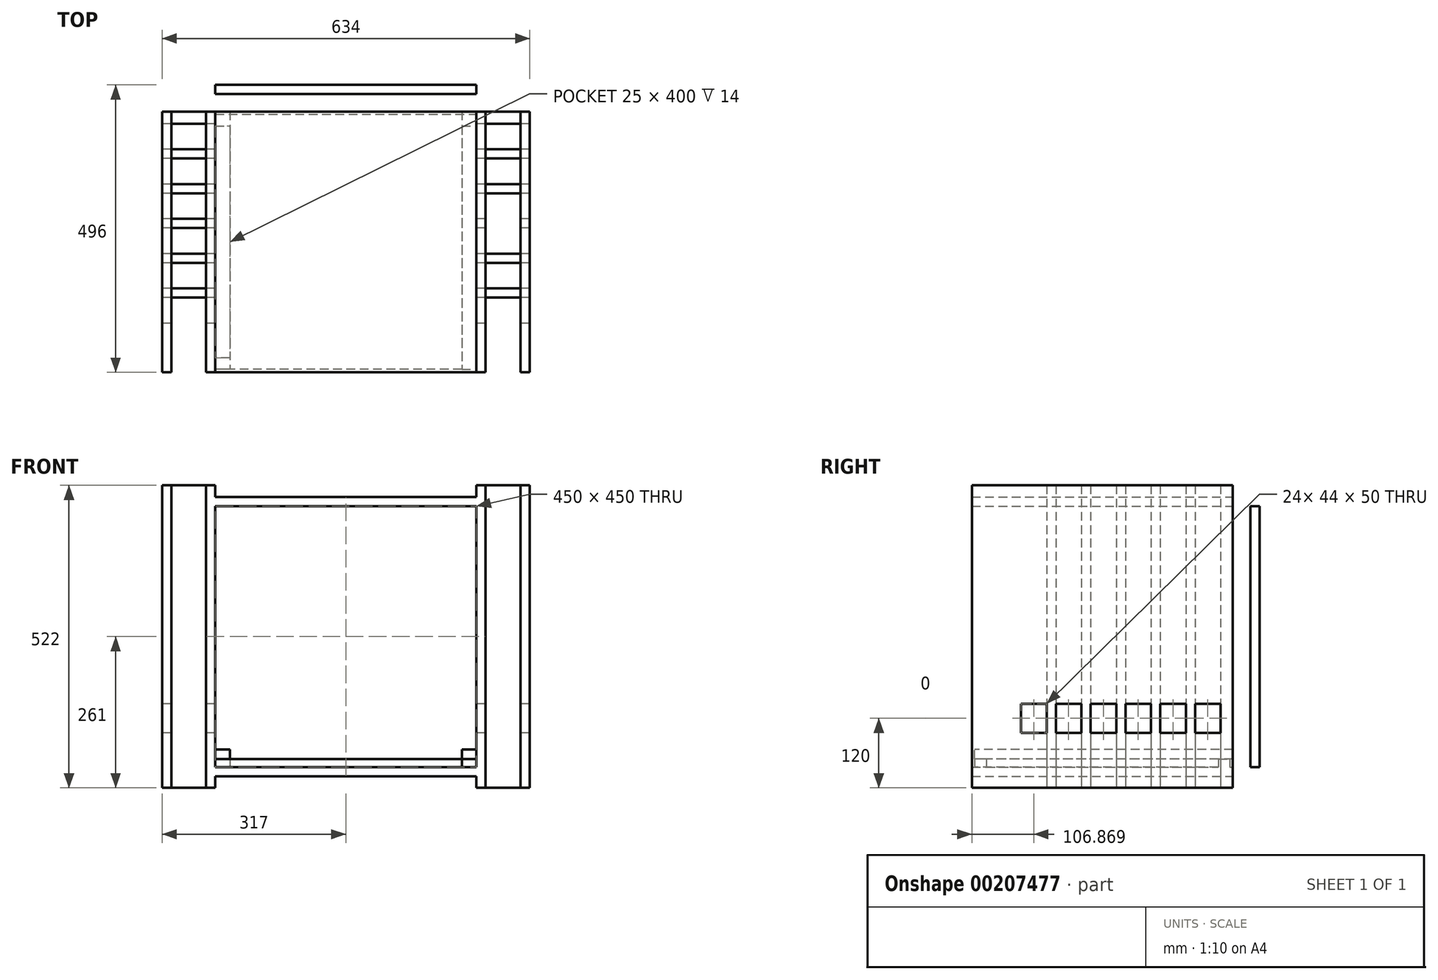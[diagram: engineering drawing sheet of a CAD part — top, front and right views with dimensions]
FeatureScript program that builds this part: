
annotation { "Feature Type Name" : "Feature", "Feature Type Description" : "" }
export const myFeature = defineFeature(function(context is Context, id is Id, definition is map)
    precondition{}
    {
        {
            var Q0;
            Q0=qCreatedBy(makeId("Front.planeOp"),FACE);
            var sketch = newSketch(context, id + "F0", { "sketchPlane" : qUnion([Q0])});
            skLineSegment(sketch, "E0.bottom", {"start": v(0, 0) * mm, "end": v(1200, 0) * mm, "construction": true});
            skLineSegment(sketch, "E0.top", {"start": v(0, 1200) * mm, "end": v(1200, 1200) * mm, "construction": true});
            skLineSegment(sketch, "E0.left", {"start": v(0, 0) * mm, "end": v(0, 1200) * mm, "construction": true});
            skLineSegment(sketch, "E0.right", {"start": v(1200, 0) * mm, "end": v(1200, 1200) * mm, "construction": true});
            skLineSegment(sketch, "E1.bottom", {"start": v(0, 0) * mm, "end": v(50, 0) * mm, "construction": true});
            skLineSegment(sketch, "E1.top", {"start": v(0, 50) * mm, "end": v(50, 50) * mm, "construction": true});
            skLineSegment(sketch, "E1.left", {"start": v(0, 0) * mm, "end": v(0, 50) * mm, "construction": true});
            skLineSegment(sketch, "E1.right", {"start": v(50, 0) * mm, "end": v(50, 50) * mm, "construction": true});
            skPoint(sketch, "E2", {"position": v(50, 50) * mm});
            skLineSegment(sketch, "E3", {"start": v(-443.22, -344.23) * mm, "end": v(-427.22, -344.23) * mm, "construction": true});
            skLineSegment(sketch, "E4", {"start": v(-345.47, -205) * mm, "end": v(-345.47, -221) * mm, "construction": true});
            skLineSegment(sketch, "E5", {"start": v(-341.02, 423.4) * mm, "end": v(-341.02, 407.4) * mm, "construction": true});
            skLineSegment(sketch, "E6", {"start": v(1457.06, 1178.81) * mm, "end": v(1457.06, 1162.81) * mm, "construction": true});
            skLineSegment(sketch, "E7", {"start": v(781.58, 762.66) * mm, "end": v(797.58, 762.66) * mm, "construction": true});
            skSolve(sketch);
        }
        {
            var Q0;
            Q0=qCreatedBy(makeId("Front.planeOp"),FACE);
            var sketch = newSketch(context, id + "F1", { "sketchPlane" : qUnion([Q0])});
            skLineSegment(sketch, "E8.bottom", {"start": v(50, 50) * mm, "end": v(66, 50) * mm});
            skLineSegment(sketch, "E8.top", {"start": v(50, 572) * mm, "end": v(66, 572) * mm});
            skLineSegment(sketch, "E8.left", {"start": v(50, 50) * mm, "end": v(50, 572) * mm});
            skLineSegment(sketch, "E8.right", {"start": v(66, 50) * mm, "end": v(66, 572) * mm});
            skLineSegment(sketch, "E9.bottom", {"start": v(66, 536) * mm, "end": v(516, 536) * mm});
            skLineSegment(sketch, "E9.top", {"start": v(66, 552) * mm, "end": v(516, 552) * mm});
            skLineSegment(sketch, "E9.left", {"start": v(66, 536) * mm, "end": v(66, 552) * mm});
            skLineSegment(sketch, "E9.right", {"start": v(516, 536) * mm, "end": v(516, 552) * mm});
            skLineSegment(sketch, "E10.bottom", {"start": v(66, 70) * mm, "end": v(516, 70) * mm});
            skLineSegment(sketch, "E10.top", {"start": v(66, 86) * mm, "end": v(516, 86) * mm});
            skLineSegment(sketch, "E10.left", {"start": v(66, 70) * mm, "end": v(66, 86) * mm});
            skLineSegment(sketch, "E10.right", {"start": v(516, 70) * mm, "end": v(516, 86) * mm});
            skLineSegment(sketch, "E11.bottom", {"start": v(-10, 572) * mm, "end": v(-26, 572) * mm});
            skLineSegment(sketch, "E11.top", {"start": v(-10, 50) * mm, "end": v(-26, 50) * mm});
            skLineSegment(sketch, "E11.left", {"start": v(-10, 572) * mm, "end": v(-10, 50) * mm});
            skLineSegment(sketch, "E11.right", {"start": v(-26, 572) * mm, "end": v(-26, 50) * mm});
            skLineSegment(sketch, "E12", {"start": v(291, -118.69) * mm, "end": v(291, -340.53) * mm, "construction": true});
            skPoint(sketch, "E12.startSnap0", {"position": v(291, 70) * mm});
            skLineSegment(sketch, "E13.MirrorCS", {"start": v(516, 50) * mm, "end": v(516, 572) * mm});
            skLineSegment(sketch, "E14.MirrorCS", {"start": v(532, 50) * mm, "end": v(532, 572) * mm});
            skLineSegment(sketch, "E15.MirrorCS", {"start": v(532, 572) * mm, "end": v(516, 572) * mm});
            skLineSegment(sketch, "E16.MirrorCS", {"start": v(532, 50) * mm, "end": v(516, 50) * mm});
            skLineSegment(sketch, "E17.MirrorCS", {"start": v(592, 572) * mm, "end": v(592, 50) * mm});
            skLineSegment(sketch, "E18.MirrorCS", {"start": v(592, 50) * mm, "end": v(608, 50) * mm});
            skLineSegment(sketch, "E19.MirrorCS", {"start": v(592, 572) * mm, "end": v(608, 572) * mm});
            skLineSegment(sketch, "E20.MirrorCS", {"start": v(608, 572) * mm, "end": v(608, 50) * mm});
            skPoint(sketch, "E21", {"position": v(66, 692.57) * mm});
            skPoint(sketch, "E22", {"position": v(66, 311) * mm});
            skSolve(sketch);
        }
        {
            var Q0;
            Q0=qCreatedBy(makeId("Top.planeOp"),FACE);
            var sketch = newSketch(context, id + "F2", { "sketchPlane" : qUnion([Q0])});
            skLineSegment(sketch, "E23.bottom", {"start": v(50, 0) * mm, "end": v(66, 0) * mm});
            skLineSegment(sketch, "E23.top", {"start": v(50, -450) * mm, "end": v(66, -450) * mm});
            skLineSegment(sketch, "E23.left", {"start": v(50, 0) * mm, "end": v(50, -450) * mm});
            skLineSegment(sketch, "E23.right", {"start": v(66, 0) * mm, "end": v(66, -450) * mm});
            skLineSegment(sketch, "E24", {"start": v(291, -589.17) * mm, "end": v(291, -887.41) * mm, "construction": true});
            skLineSegment(sketch, "E25.MirrorCS", {"start": v(516, 0) * mm, "end": v(516, -450) * mm});
            skLineSegment(sketch, "E26.MirrorCS", {"start": v(532, 0) * mm, "end": v(532, -450) * mm});
            skLineSegment(sketch, "E27.MirrorCS", {"start": v(532, -450) * mm, "end": v(516, -450) * mm});
            skLineSegment(sketch, "E28.MirrorCS", {"start": v(532, 0) * mm, "end": v(516, 0) * mm});
            skSolve(sketch);
        }
        {
            var Q0;
            {var subQ0=sQuery(id+"F1.wireOp",EDGE,"E10.bottom");Q0=makeQuery(id+"F1.imprint","IMPRINT",FACE,{"disambiguationData":[TD([[makeQuery(id+"F1.imprint","IMPRINT",EDGE,{"derivedFrom":subQ0}),1.0]])]});}
            var Q1;
            Q1=makeQuery(id+"F1.imprint","IMPRINT",FACE,{"disambiguationData":[TD([[makeQuery(id+"F1.imprint","IMPRINT",EDGE,{"derivedFrom":sQuery(id+"F1.wireOp",EDGE,"E14.MirrorCS")}),1.0]])]});
            var Q2;
            {var subQ0=sQuery(id+"F1.wireOp",EDGE,"E9.bottom");Q2=makeQuery(id+"F1.imprint","IMPRINT",FACE,{"disambiguationData":[TD([[makeQuery(id+"F1.imprint","IMPRINT",EDGE,{"derivedFrom":subQ0}),1.0]])]});}
            var Q3;
            Q3=makeQuery(id+"F1.imprint","IMPRINT",FACE,{"disambiguationData":[TD([[makeQuery(id+"F1.imprint","IMPRINT",EDGE,{"derivedFrom":sQuery(id+"F1.wireOp",EDGE,"E17.MirrorCS")}),1.0]])]});
            var Q4;
            {var subQ1=sQuery(id+"F1.wireOp",EDGE,"E8.bottom");Q4=makeQuery(id+"F1.imprint","IMPRINT",FACE,{"disambiguationData":[TD([[makeQuery(id+"F1.imprint","IMPRINT",EDGE,{"derivedFrom":subQ1}),1.0]])]});}
            var Q5;
            Q5=makeQuery(id+"F1.imprint","IMPRINT",FACE,{"disambiguationData":[TD([[makeQuery(id+"F1.imprint","IMPRINT",EDGE,{"derivedFrom":sQuery(id+"F1.wireOp",EDGE,"E11.bottom")}),1.0]])]});
            var Q6;
            Q6=sQuery(id+"F2.wireOp",VERTEX,"E23.left.end");
            extrude(context, id + "F3", {"entities" : qUnion([Q0, Q1, Q2, Q3, Q4, Q5]), "endBound" : BoundingType.UP_TO_VERTEX, "endBoundEntityVertex" : qUnion([Q6]), "depth" : 25 * mm});
        }
        {
            var Q0;
            Q0=qCreatedBy(makeId("Right.planeOp"),FACE);
            var sketch = newSketch(context, id + "F4", { "sketchPlane" : qUnion([Q0])});
            skLineSegment(sketch, "E29.bottom", {"start": v(0, 145) * mm, "end": v(-450, 145) * mm});
            skLineSegment(sketch, "E29.top", {"start": v(0, 195) * mm, "end": v(-450, 195) * mm});
            skLineSegment(sketch, "E29.left", {"start": v(0, 145) * mm, "end": v(0, 195) * mm});
            skLineSegment(sketch, "E29.right", {"start": v(-450, 145) * mm, "end": v(-450, 195) * mm});
            skPoint(sketch, "E30", {"position": v(0, 170) * mm});
            skLineSegment(sketch, "E31.bottom", {"start": v(-5.13, 195) * mm, "end": v(-21.13, 195) * mm});
            skLineSegment(sketch, "E31.top", {"start": v(-5.13, 145) * mm, "end": v(-21.13, 145) * mm});
            skLineSegment(sketch, "E31.left", {"start": v(-5.13, 195) * mm, "end": v(-5.13, 145) * mm});
            skLineSegment(sketch, "E31.right", {"start": v(-21.13, 195) * mm, "end": v(-21.13, 145) * mm});
            skLineSegment(sketch, "E32.1.0.0", {"start": v(-81.13, 195) * mm, "end": v(-81.13, 145) * mm});
            skLineSegment(sketch, "E32.1.0.1", {"start": v(-65.13, 195) * mm, "end": v(-65.13, 145) * mm});
            skLineSegment(sketch, "E32.2.0.0", {"start": v(-141.13, 195) * mm, "end": v(-141.13, 145) * mm});
            skLineSegment(sketch, "E32.2.0.1", {"start": v(-125.13, 195) * mm, "end": v(-125.13, 145) * mm});
            skLineSegment(sketch, "E32.3.0.0", {"start": v(-201.13, 195) * mm, "end": v(-201.13, 145) * mm});
            skLineSegment(sketch, "E32.3.0.1", {"start": v(-185.13, 195) * mm, "end": v(-185.13, 145) * mm});
            skLineSegment(sketch, "E32.4.0.0", {"start": v(-261.13, 195) * mm, "end": v(-261.13, 145) * mm});
            skLineSegment(sketch, "E32.4.0.1", {"start": v(-245.13, 195) * mm, "end": v(-245.13, 145) * mm});
            skLineSegment(sketch, "E32.5.0.0", {"start": v(-321.13, 195) * mm, "end": v(-321.13, 145) * mm});
            skLineSegment(sketch, "E32.5.0.1", {"start": v(-305.13, 195) * mm, "end": v(-305.13, 145) * mm});
            skLineSegment(sketch, "E32.direction1", {"start": v(-21.13, 145) * mm, "end": v(-81.13, 145) * mm, "construction": true});
            skLineSegment(sketch, "E33.0.6.0", {"start": v(-381.13, 195) * mm, "end": v(-381.13, 145) * mm});
            skLineSegment(sketch, "E33.3.6.0", {"start": v(-365.13, 195) * mm, "end": v(-365.13, 145) * mm});
            skSolve(sketch);
        }
        {
            var Q0;
            {var subQ0=sQuery(id+"F4.wireOp",EDGE,"E31.right");Q0=makeQuery(id+"F4.imprint","IMPRINT",FACE,{"disambiguationData":[TD([[makeQuery(id+"F4.imprint","IMPRINT",EDGE,{"derivedFrom":subQ0}),-1.0]])]});}
            var Q1;
            {var subQ0=sQuery(id+"F4.wireOp",EDGE,"E32.1.0.0");Q1=makeQuery(id+"F4.imprint","IMPRINT",FACE,{"disambiguationData":[TD([[makeQuery(id+"F4.imprint","IMPRINT",EDGE,{"derivedFrom":subQ0}),-1.0]])]});}
            var Q2;
            {var subQ0=sQuery(id+"F4.wireOp",EDGE,"E32.2.0.0");Q2=makeQuery(id+"F4.imprint","IMPRINT",FACE,{"disambiguationData":[TD([[makeQuery(id+"F4.imprint","IMPRINT",EDGE,{"derivedFrom":subQ0}),-1.0]])]});}
            var Q3;
            {var subQ0=sQuery(id+"F4.wireOp",EDGE,"E32.3.0.0");Q3=makeQuery(id+"F4.imprint","IMPRINT",FACE,{"disambiguationData":[TD([[makeQuery(id+"F4.imprint","IMPRINT",EDGE,{"derivedFrom":subQ0}),-1.0]])]});}
            var Q4;
            {var subQ0=sQuery(id+"F4.wireOp",EDGE,"E32.4.0.0");Q4=makeQuery(id+"F4.imprint","IMPRINT",FACE,{"disambiguationData":[TD([[makeQuery(id+"F4.imprint","IMPRINT",EDGE,{"derivedFrom":subQ0}),-1.0]])]});}
            var Q5;
            {var subQ0=sQuery(id+"F4.wireOp",EDGE,"E32.5.0.0");Q5=makeQuery(id+"F4.imprint","IMPRINT",FACE,{"disambiguationData":[TD([[makeQuery(id+"F4.imprint","IMPRINT",EDGE,{"derivedFrom":subQ0}),-1.0]])]});}
            extrude(context, id + "F5", {"entities" : qUnion([Q0, Q1, Q2, Q3, Q4, Q5]), "operationType" : NewBodyOperationType.REMOVE, "depth" : 1209 * mm, "hasSecondDirection" : true, "secondDirectionOppositeDirection" : true, "secondDirectionDepth" : 175 * mm});
        }
        {
            var Q0;
            Q0=qCreatedBy(makeId("Top.planeOp"),FACE);
            var sketch = newSketch(context, id + "F6", { "sketchPlane" : qUnion([Q0])});
            skLineSegment(sketch, "E34.bottom", {"start": v(-10, -21.13) * mm, "end": v(50, -21.13) * mm});
            skLineSegment(sketch, "E34.top", {"start": v(-10, -65.13) * mm, "end": v(50, -65.13) * mm});
            skLineSegment(sketch, "E34.left", {"start": v(50, -21.13) * mm, "end": v(50, -65.13) * mm});
            skLineSegment(sketch, "E34.right", {"start": v(-10, -21.13) * mm, "end": v(-10, -65.13) * mm});
            skLineSegment(sketch, "E35.bottom", {"start": v(-10, -81.13) * mm, "end": v(50, -81.13) * mm});
            skLineSegment(sketch, "E35.top", {"start": v(-10, -125.13) * mm, "end": v(50, -125.13) * mm});
            skLineSegment(sketch, "E35.left", {"start": v(50, -81.13) * mm, "end": v(50, -125.13) * mm});
            skLineSegment(sketch, "E35.right", {"start": v(-10, -81.13) * mm, "end": v(-10, -125.13) * mm});
            skLineSegment(sketch, "E36.bottom", {"start": v(50, -141.13) * mm, "end": v(-10, -141.13) * mm});
            skLineSegment(sketch, "E36.top", {"start": v(50, -185.13) * mm, "end": v(-10, -185.13) * mm});
            skLineSegment(sketch, "E36.left", {"start": v(-10, -141.13) * mm, "end": v(-10, -185.13) * mm});
            skLineSegment(sketch, "E36.right", {"start": v(50, -141.13) * mm, "end": v(50, -185.13) * mm});
            skLineSegment(sketch, "E37.bottom", {"start": v(-10, -201.13) * mm, "end": v(50, -201.13) * mm});
            skLineSegment(sketch, "E37.top", {"start": v(-10, -245.13) * mm, "end": v(50, -245.13) * mm});
            skLineSegment(sketch, "E37.left", {"start": v(50, -201.13) * mm, "end": v(50, -245.13) * mm});
            skLineSegment(sketch, "E37.right", {"start": v(-10, -201.13) * mm, "end": v(-10, -245.13) * mm});
            skLineSegment(sketch, "E38.bottom", {"start": v(-10, -261.13) * mm, "end": v(50, -261.13) * mm});
            skLineSegment(sketch, "E38.top", {"start": v(-10, -305.13) * mm, "end": v(50, -305.13) * mm});
            skLineSegment(sketch, "E38.left", {"start": v(50, -261.13) * mm, "end": v(50, -305.13) * mm});
            skLineSegment(sketch, "E38.right", {"start": v(-10, -261.13) * mm, "end": v(-10, -305.13) * mm});
            skLineSegment(sketch, "E39.bottom", {"start": v(-10, -321.13) * mm, "end": v(50, -321.13) * mm});
            skLineSegment(sketch, "E39.top", {"start": v(-10, -365.13) * mm, "end": v(50, -365.13) * mm});
            skLineSegment(sketch, "E39.left", {"start": v(50, -321.13) * mm, "end": v(50, -365.13) * mm});
            skLineSegment(sketch, "E39.right", {"start": v(-10, -321.13) * mm, "end": v(-10, -365.13) * mm});
            skLineSegment(sketch, "E40.bottom", {"start": v(50, 0) * mm, "end": v(-10, 0) * mm});
            skLineSegment(sketch, "E40.top", {"start": v(50, -450) * mm, "end": v(-10, -450) * mm});
            skLineSegment(sketch, "E40.left", {"start": v(50, 0) * mm, "end": v(50, -450) * mm});
            skLineSegment(sketch, "E40.right", {"start": v(-10, 0) * mm, "end": v(-10, -450) * mm});
            skLineSegment(sketch, "E41.MirrorCS", {"start": v(532, -450) * mm, "end": v(592, -450) * mm});
            skLineSegment(sketch, "E42.MirrorCS", {"start": v(592, -365.13) * mm, "end": v(532, -365.13) * mm});
            skLineSegment(sketch, "E43.MirrorCS", {"start": v(592, -321.13) * mm, "end": v(532, -321.13) * mm});
            skLineSegment(sketch, "E44.MirrorCS", {"start": v(592, -305.13) * mm, "end": v(532, -305.13) * mm});
            skLineSegment(sketch, "E45.MirrorCS", {"start": v(592, -261.13) * mm, "end": v(532, -261.13) * mm});
            skLineSegment(sketch, "E46.MirrorCS", {"start": v(592, -245.13) * mm, "end": v(532, -245.13) * mm});
            skLineSegment(sketch, "E47.MirrorCS", {"start": v(592, -201.13) * mm, "end": v(532, -201.13) * mm});
            skLineSegment(sketch, "E48.MirrorCS", {"start": v(532, -141.13) * mm, "end": v(592, -141.13) * mm});
            skLineSegment(sketch, "E49.MirrorCS", {"start": v(592, -125.13) * mm, "end": v(532, -125.13) * mm});
            skLineSegment(sketch, "E50.MirrorCS", {"start": v(592, -81.13) * mm, "end": v(532, -81.13) * mm});
            skLineSegment(sketch, "E51.MirrorCS", {"start": v(592, -65.13) * mm, "end": v(532, -65.13) * mm});
            skLineSegment(sketch, "E52.MirrorCS", {"start": v(592, -21.13) * mm, "end": v(532, -21.13) * mm});
            skLineSegment(sketch, "E53.MirrorCS", {"start": v(532, 0) * mm, "end": v(592, 0) * mm});
            skLineSegment(sketch, "E54.MirrorCS", {"start": v(592, 0) * mm, "end": v(592, -450) * mm});
            skLineSegment(sketch, "E55.MirrorCS", {"start": v(532, 0) * mm, "end": v(532, -450) * mm});
            skSolve(sketch);
        }
        {
            var Q0;
            {var subQ0=sQuery(id+"F6.wireOp",EDGE,"E34.bottom");Q0=makeQuery(id+"F6.imprint","IMPRINT",FACE,{"disambiguationData":[TD([[makeQuery(id+"F6.imprint","IMPRINT",EDGE,{"derivedFrom":subQ0}),1.0]])]});}
            var Q1;
            {var subQ0=sQuery(id+"F6.wireOp",EDGE,"E34.top");Q1=makeQuery(id+"F6.imprint","IMPRINT",FACE,{"disambiguationData":[TD([[makeQuery(id+"F6.imprint","IMPRINT",EDGE,{"derivedFrom":subQ0}),-1.0]])]});}
            var Q2;
            {var subQ0=sQuery(id+"F6.wireOp",EDGE,"E35.top");Q2=makeQuery(id+"F6.imprint","IMPRINT",FACE,{"disambiguationData":[TD([[makeQuery(id+"F6.imprint","IMPRINT",EDGE,{"derivedFrom":subQ0}),-1.0]])]});}
            var Q3;
            {var subQ0=sQuery(id+"F6.wireOp",EDGE,"E36.top");Q3=makeQuery(id+"F6.imprint","IMPRINT",FACE,{"disambiguationData":[TD([[makeQuery(id+"F6.imprint","IMPRINT",EDGE,{"derivedFrom":subQ0}),1.0]])]});}
            var Q4;
            {var subQ0=sQuery(id+"F6.wireOp",EDGE,"E37.top");Q4=makeQuery(id+"F6.imprint","IMPRINT",FACE,{"disambiguationData":[TD([[makeQuery(id+"F6.imprint","IMPRINT",EDGE,{"derivedFrom":subQ0}),-1.0]])]});}
            var Q5;
            {var subQ0=sQuery(id+"F6.wireOp",EDGE,"E38.top");Q5=makeQuery(id+"F6.imprint","IMPRINT",FACE,{"disambiguationData":[TD([[makeQuery(id+"F6.imprint","IMPRINT",EDGE,{"derivedFrom":subQ0}),-1.0]])]});}
            var Q6;
            {var subQ0=sQuery(id+"F6.wireOp",EDGE,"E43.MirrorCS");Q6=makeQuery(id+"F6.imprint","IMPRINT",FACE,{"disambiguationData":[TD([[makeQuery(id+"F6.imprint","IMPRINT",EDGE,{"derivedFrom":subQ0}),-1.0]])]});}
            var Q7;
            {var subQ0=sQuery(id+"F6.wireOp",EDGE,"E45.MirrorCS");Q7=makeQuery(id+"F6.imprint","IMPRINT",FACE,{"disambiguationData":[TD([[makeQuery(id+"F6.imprint","IMPRINT",EDGE,{"derivedFrom":subQ0}),-1.0]])]});}
            var Q8;
            {var subQ0=sQuery(id+"F6.wireOp",EDGE,"E48.MirrorCS");Q8=makeQuery(id+"F6.imprint","IMPRINT",FACE,{"disambiguationData":[TD([[makeQuery(id+"F6.imprint","IMPRINT",EDGE,{"derivedFrom":subQ0}),1.0]])]});}
            var Q9;
            {var subQ0=sQuery(id+"F6.wireOp",EDGE,"E50.MirrorCS");Q9=makeQuery(id+"F6.imprint","IMPRINT",FACE,{"disambiguationData":[TD([[makeQuery(id+"F6.imprint","IMPRINT",EDGE,{"derivedFrom":subQ0}),-1.0]])]});}
            var Q10;
            {var subQ0=sQuery(id+"F6.wireOp",EDGE,"E52.MirrorCS");Q10=makeQuery(id+"F6.imprint","IMPRINT",FACE,{"disambiguationData":[TD([[makeQuery(id+"F6.imprint","IMPRINT",EDGE,{"derivedFrom":subQ0}),-1.0]])]});}
            var Q11;
            Q11=makeQuery(id+"F3.opExtrude","SWEPT_FACE",FACE,{"disambiguationData":[OSD([sQuery(id+"F1.wireOp",EDGE,"E11.bottom")])]});
            var Q12;
            Q12=makeQuery(id+"F3.opExtrude","SWEPT_BODY",BODY,{"disambiguationData":[OSD([sQuery(id+"F1.wireOp",EDGE,"E11.bottom"),sQuery(id+"F1.wireOp",EDGE,"E11.top"),sQuery(id+"F1.wireOp",EDGE,"E11.left"),sQuery(id+"F1.wireOp",EDGE,"E11.right")])]});
            var Q13;
            Q13=makeQuery(id+"F3.opExtrude","CAP_VERTEX",VERTEX,{"disambiguationData":[OSD([sQuery(id+"F1.wireOp",EDGE,"E11.top"),sQuery(id+"F1.wireOp",EDGE,"E11.left")])],"isStart":true});
            extrude(context, id + "F7", {"entities" : qUnion([Q0, Q1, Q2, Q3, Q4, Q5, Q6, Q7, Q8, Q9, Q10]), "endBound" : BoundingType.UP_TO_SURFACE, "endBoundEntityFace" : qUnion([Q11]), "depth" : 441 * mm});
        }
        {
            var Q0;
            Q0=makeQuery(id+"F7.opExtrude","CAP_FACE",FACE,{"disambiguationData":[OSD([sQuery(id+"F6.wireOp",EDGE,"E34.bottom"),sQuery(id+"F6.wireOp",EDGE,"E40.bottom"),sQuery(id+"F6.wireOp",EDGE,"E40.left"),sQuery(id+"F6.wireOp",EDGE,"E40.right")])],"isStart":true});
            var Q1;
            Q1=makeQuery(id+"F7.opExtrude","CAP_FACE",FACE,{"disambiguationData":[OSD([sQuery(id+"F6.wireOp",EDGE,"E34.top"),sQuery(id+"F6.wireOp",EDGE,"E35.bottom"),sQuery(id+"F6.wireOp",EDGE,"E40.left"),sQuery(id+"F6.wireOp",EDGE,"E40.right")])],"isStart":true});
            var Q2;
            Q2=makeQuery(id+"F7.opExtrude","CAP_FACE",FACE,{"disambiguationData":[OSD([sQuery(id+"F6.wireOp",EDGE,"E35.top"),sQuery(id+"F6.wireOp",EDGE,"E36.bottom"),sQuery(id+"F6.wireOp",EDGE,"E40.left"),sQuery(id+"F6.wireOp",EDGE,"E40.right")])],"isStart":true});
            var Q3;
            Q3=makeQuery(id+"F7.opExtrude","CAP_FACE",FACE,{"disambiguationData":[OSD([sQuery(id+"F6.wireOp",EDGE,"E36.top"),sQuery(id+"F6.wireOp",EDGE,"E37.bottom"),sQuery(id+"F6.wireOp",EDGE,"E40.left"),sQuery(id+"F6.wireOp",EDGE,"E40.right")])],"isStart":true});
            var Q4;
            Q4=makeQuery(id+"F7.opExtrude","CAP_FACE",FACE,{"disambiguationData":[OSD([sQuery(id+"F6.wireOp",EDGE,"E37.top"),sQuery(id+"F6.wireOp",EDGE,"E38.bottom"),sQuery(id+"F6.wireOp",EDGE,"E40.left"),sQuery(id+"F6.wireOp",EDGE,"E40.right")])],"isStart":true});
            var Q5;
            Q5=makeQuery(id+"F7.opExtrude","CAP_FACE",FACE,{"disambiguationData":[OSD([sQuery(id+"F6.wireOp",EDGE,"E38.top"),sQuery(id+"F6.wireOp",EDGE,"E39.bottom"),sQuery(id+"F6.wireOp",EDGE,"E40.left"),sQuery(id+"F6.wireOp",EDGE,"E40.right")])],"isStart":true});
            var Q6;
            Q6=makeQuery(id+"F7.opExtrude","CAP_FACE",FACE,{"disambiguationData":[OSD([sQuery(id+"F6.wireOp",EDGE,"E52.MirrorCS"),sQuery(id+"F6.wireOp",EDGE,"E53.MirrorCS"),sQuery(id+"F6.wireOp",EDGE,"E54.MirrorCS"),sQuery(id+"F6.wireOp",EDGE,"E55.MirrorCS")])],"isStart":true});
            var Q7;
            Q7=makeQuery(id+"F7.opExtrude","CAP_FACE",FACE,{"disambiguationData":[OSD([sQuery(id+"F6.wireOp",EDGE,"E50.MirrorCS"),sQuery(id+"F6.wireOp",EDGE,"E51.MirrorCS"),sQuery(id+"F6.wireOp",EDGE,"E54.MirrorCS"),sQuery(id+"F6.wireOp",EDGE,"E55.MirrorCS")])],"isStart":true});
            var Q8;
            Q8=makeQuery(id+"F7.opExtrude","CAP_FACE",FACE,{"disambiguationData":[OSD([sQuery(id+"F6.wireOp",EDGE,"E48.MirrorCS"),sQuery(id+"F6.wireOp",EDGE,"E49.MirrorCS"),sQuery(id+"F6.wireOp",EDGE,"E54.MirrorCS"),sQuery(id+"F6.wireOp",EDGE,"E55.MirrorCS")])],"isStart":true});
            var Q9;
            Q9=makeQuery(id+"F7.opExtrude","CAP_FACE",FACE,{"disambiguationData":[OSD([sQuery(id+"F6.wireOp",EDGE,"E45.MirrorCS"),sQuery(id+"F6.wireOp",EDGE,"E46.MirrorCS"),sQuery(id+"F6.wireOp",EDGE,"E54.MirrorCS"),sQuery(id+"F6.wireOp",EDGE,"E55.MirrorCS")])],"isStart":true});
            var Q10;
            Q10=makeQuery(id+"F7.opExtrude","CAP_FACE",FACE,{"disambiguationData":[OSD([sQuery(id+"F6.wireOp",EDGE,"E43.MirrorCS"),sQuery(id+"F6.wireOp",EDGE,"E44.MirrorCS"),sQuery(id+"F6.wireOp",EDGE,"E54.MirrorCS"),sQuery(id+"F6.wireOp",EDGE,"E55.MirrorCS")])],"isStart":true});
            var Q11;
            Q11=makeQuery(id+"F3.opExtrude","SWEPT_FACE",FACE,{"disambiguationData":[OSD([sQuery(id+"F1.wireOp",EDGE,"E11.top")])]});
            extrude(context, id + "F8", {"entities" : qUnion([Q0, Q1, Q2, Q3, Q4, Q5, Q6, Q7, Q8, Q9, Q10]), "operationType" : NewBodyOperationType.REMOVE, "endBound" : BoundingType.UP_TO_SURFACE, "oppositeDirection" : true, "endBoundEntityFace" : qUnion([Q11]), "depth" : 25 * mm});
        }
        {
            var Q0;
            {var subQ0=sQuery(id+"F1.wireOp",EDGE,"E9.bottom");Q0=makeQuery(id+"F1.imprint","IMPRINT",FACE,{"disambiguationData":[TD([[makeQuery(id+"F1.imprint","IMPRINT",EDGE,{"derivedFrom":subQ0}),-1.0]])]});}
            extrude(context, id + "F9", {"entities" : qUnion([Q0]), "oppositeDirection" : true, "depth" : 46 * mm, "hasSecondDirection" : true, "secondDirectionOppositeDirection" : true, "secondDirectionDepth" : 30 * mm});
        }
        {
            var Q0;
            Q0=qCreatedBy(makeId("Top.planeOp"),FACE);
            var sketch = newSketch(context, id + "F10", { "sketchPlane" : qUnion([Q0])});
            skLineSegment(sketch, "E56.bottom", {"start": v(66, -25) * mm, "end": v(516, -25) * mm});
            skLineSegment(sketch, "E56.top", {"start": v(66, -5) * mm, "end": v(516, -5) * mm});
            skLineSegment(sketch, "E56.left", {"start": v(66, -25) * mm, "end": v(66, -5) * mm});
            skLineSegment(sketch, "E56.right", {"start": v(516, -25) * mm, "end": v(516, -5) * mm});
            skPoint(sketch, "E57", {"position": v(291, -5) * mm});
            skLineSegment(sketch, "E58.bottom", {"start": v(91, -445) * mm, "end": v(491, -445) * mm});
            skLineSegment(sketch, "E58.top", {"start": v(91, -25) * mm, "end": v(491, -25) * mm});
            skLineSegment(sketch, "E58.left", {"start": v(91, -25) * mm, "end": v(91, -445) * mm});
            skLineSegment(sketch, "E58.right", {"start": v(491, -25) * mm, "end": v(491, -445) * mm});
            skPoint(sketch, "E59", {"position": v(291, -25) * mm});
            skLineSegment(sketch, "E60.bottom", {"start": v(66, -25) * mm, "end": v(91, -25) * mm});
            skLineSegment(sketch, "E60.top", {"start": v(66, -445) * mm, "end": v(91, -445) * mm});
            skLineSegment(sketch, "E60.left", {"start": v(66, -25) * mm, "end": v(66, -445) * mm});
            skLineSegment(sketch, "E61.bottom", {"start": v(516, -25) * mm, "end": v(491, -25) * mm});
            skLineSegment(sketch, "E61.top", {"start": v(516, -445) * mm, "end": v(491, -445) * mm});
            skLineSegment(sketch, "E61.left", {"start": v(516, -25) * mm, "end": v(516, -445) * mm});
            skLineSegment(sketch, "E62.top", {"start": v(66, -425) * mm, "end": v(91, -425) * mm});
            skLineSegment(sketch, "E62.left", {"start": v(66, -445) * mm, "end": v(66, -425) * mm});
            skLineSegment(sketch, "E62.right", {"start": v(91, -445) * mm, "end": v(91, -425) * mm});
            skLineSegment(sketch, "E63.bottom", {"start": v(491, -445) * mm, "end": v(516, -445) * mm});
            skLineSegment(sketch, "E63.top", {"start": v(491, -425) * mm, "end": v(516, -425) * mm});
            skLineSegment(sketch, "E63.left", {"start": v(491, -445) * mm, "end": v(491, -425) * mm});
            skLineSegment(sketch, "E63.right", {"start": v(516, -445) * mm, "end": v(516, -425) * mm});
            skSolve(sketch);
        }
        {
            var Q0;
            Q0=makeQuery(id+"F10.imprint","IMPRINT",FACE,{"disambiguationData":[TD([[makeQuery(id+"F10.imprint","IMPRINT",EDGE,{"derivedFrom":sQuery(id+"F10.wireOp",EDGE,"E58.bottom")}),1.0]])]});
            var Q1;
            Q1=makeQuery(id+"F10.imprint","IMPRINT",FACE,{"disambiguationData":[TD([[makeQuery(id+"F10.imprint","IMPRINT",EDGE,{"derivedFrom":sQuery(id+"F10.wireOp",EDGE,"E56.top")}),-1.0]])]});
            var Q2;
            Q2=makeQuery(id+"F3.opExtrude","CAP_VERTEX",VERTEX,{"disambiguationData":[OSD([sQuery(id+"F1.wireOp",EDGE,"E8.right"),sQuery(id+"F1.wireOp",EDGE,"E10.top"),sQuery(id+"F1.wireOp",EDGE,"E10.left"),dummyQuery(id+"F3.vertexPlane.planeOp",FACE)])],"isStart":false});
            extrude(context, id + "F11", {"entities" : qUnion([Q0, Q1]), "depth" : 100 * mm, "hasSecondDirection" : true, "secondDirectionBound" : BoundingType.UP_TO_VERTEX, "secondDirectionOppositeDirection" : false, "secondDirectionBoundEntityVertex" : qUnion([Q2]), "secondDirectionDepth" : 25 * mm});
        }
        {
            var Q0;
            Q0=makeQuery(id+"F10.imprint","IMPRINT",FACE,{"disambiguationData":[TD([[makeQuery(id+"F10.imprint","IMPRINT",EDGE,{"derivedFrom":sQuery(id+"F10.wireOp",EDGE,"E60.top")}),1.0]])]});
            var Q1;
            Q1=makeQuery(id+"F10.imprint","IMPRINT",FACE,{"disambiguationData":[TD([[makeQuery(id+"F10.imprint","IMPRINT",EDGE,{"derivedFrom":sQuery(id+"F10.wireOp",EDGE,"E63.bottom")}),1.0]])]});
            var Q2;
            Q2=makeQuery(id+"F3.opExtrude","CAP_VERTEX",VERTEX,{"disambiguationData":[OSD([sQuery(id+"F1.wireOp",EDGE,"E8.right"),sQuery(id+"F1.wireOp",EDGE,"E10.bottom"),sQuery(id+"F1.wireOp",EDGE,"E10.left"),dummyQuery(id+"F3.vertexPlane.planeOp",FACE)])],"isStart":false});
            extrude(context, id + "F12", {"entities" : qUnion([Q0, Q1]), "operationType" : NewBodyOperationType.ADD, "depth" : 100 * mm, "hasSecondDirection" : true, "secondDirectionBound" : BoundingType.UP_TO_VERTEX, "secondDirectionOppositeDirection" : false, "secondDirectionBoundEntityVertex" : qUnion([Q2]), "secondDirectionDepth" : 25 * mm});
        }
        {
            var Q0;
            Q0=makeQuery(id+"F12.opExtrude","SWEPT_FACE",FACE,{"disambiguationData":[OSD([sQuery(id+"F10.wireOp",EDGE,"E60.top")])]});
            var sketch = newSketch(context, id + "F13", { "sketchPlane" : qUnion([Q0])});
            skLineSegment(sketch, "E64.bottom", {"start": v(91, 100) * mm, "end": v(66, 100) * mm});
            skLineSegment(sketch, "E64.top", {"start": v(91, 116) * mm, "end": v(66, 116) * mm});
            skLineSegment(sketch, "E64.left", {"start": v(91, 100) * mm, "end": v(91, 116) * mm});
            skLineSegment(sketch, "E64.right", {"start": v(66, 100) * mm, "end": v(66, 116) * mm});
            skLineSegment(sketch, "E65.MirrorCS", {"start": v(491, 116) * mm, "end": v(516, 116) * mm});
            skLineSegment(sketch, "E66.MirrorCS", {"start": v(516, 100) * mm, "end": v(516, 116) * mm});
            skLineSegment(sketch, "E67.MirrorCS", {"start": v(491, 100) * mm, "end": v(516, 100) * mm});
            skLineSegment(sketch, "E68.MirrorCS", {"start": v(491, 100) * mm, "end": v(491, 116) * mm});
            skSolve(sketch);
        }
        {
            var Q0;
            Q0=makeQuery(id+"F13.imprint","IMPRINT",FACE,{"disambiguationData":[TD([[makeQuery(id+"F13.imprint","IMPRINT",EDGE,{"derivedFrom":sQuery(id+"F13.wireOp",EDGE,"E64.bottom")}),1.0]])]});
            var Q1;
            Q1=makeQuery(id+"F13.imprint","IMPRINT",FACE,{"disambiguationData":[TD([[makeQuery(id+"F13.imprint","IMPRINT",EDGE,{"derivedFrom":sQuery(id+"F13.wireOp",EDGE,"E65.MirrorCS")}),-1.0]])]});
            var Q2;
            Q2=makeQuery(id+"F3.opExtrude","CAP_FACE",FACE,{"disambiguationData":[OSD([sQuery(id+"F1.wireOp",EDGE,"E8.bottom"),sQuery(id+"F1.wireOp",EDGE,"E8.top"),sQuery(id+"F1.wireOp",EDGE,"E8.left"),sQuery(id+"F1.wireOp",EDGE,"E8.right"),sQuery(id+"F1.wireOp",EDGE,"E9.bottom"),sQuery(id+"F1.wireOp",EDGE,"E9.top"),sQuery(id+"F1.wireOp",EDGE,"E10.bottom"),sQuery(id+"F1.wireOp",EDGE,"E10.top"),sQuery(id+"F1.wireOp",EDGE,"E13.MirrorCS"),sQuery(id+"F1.wireOp",EDGE,"E14.MirrorCS"),sQuery(id+"F1.wireOp",EDGE,"E15.MirrorCS"),sQuery(id+"F1.wireOp",EDGE,"E16.MirrorCS")])],"isStart":true});
            extrude(context, id + "F14", {"entities" : qUnion([Q0, Q1]), "endBound" : BoundingType.UP_TO_SURFACE, "oppositeDirection" : true, "endBoundEntityFace" : qUnion([Q2]), "depth" : 25 * mm});
        }
    });
